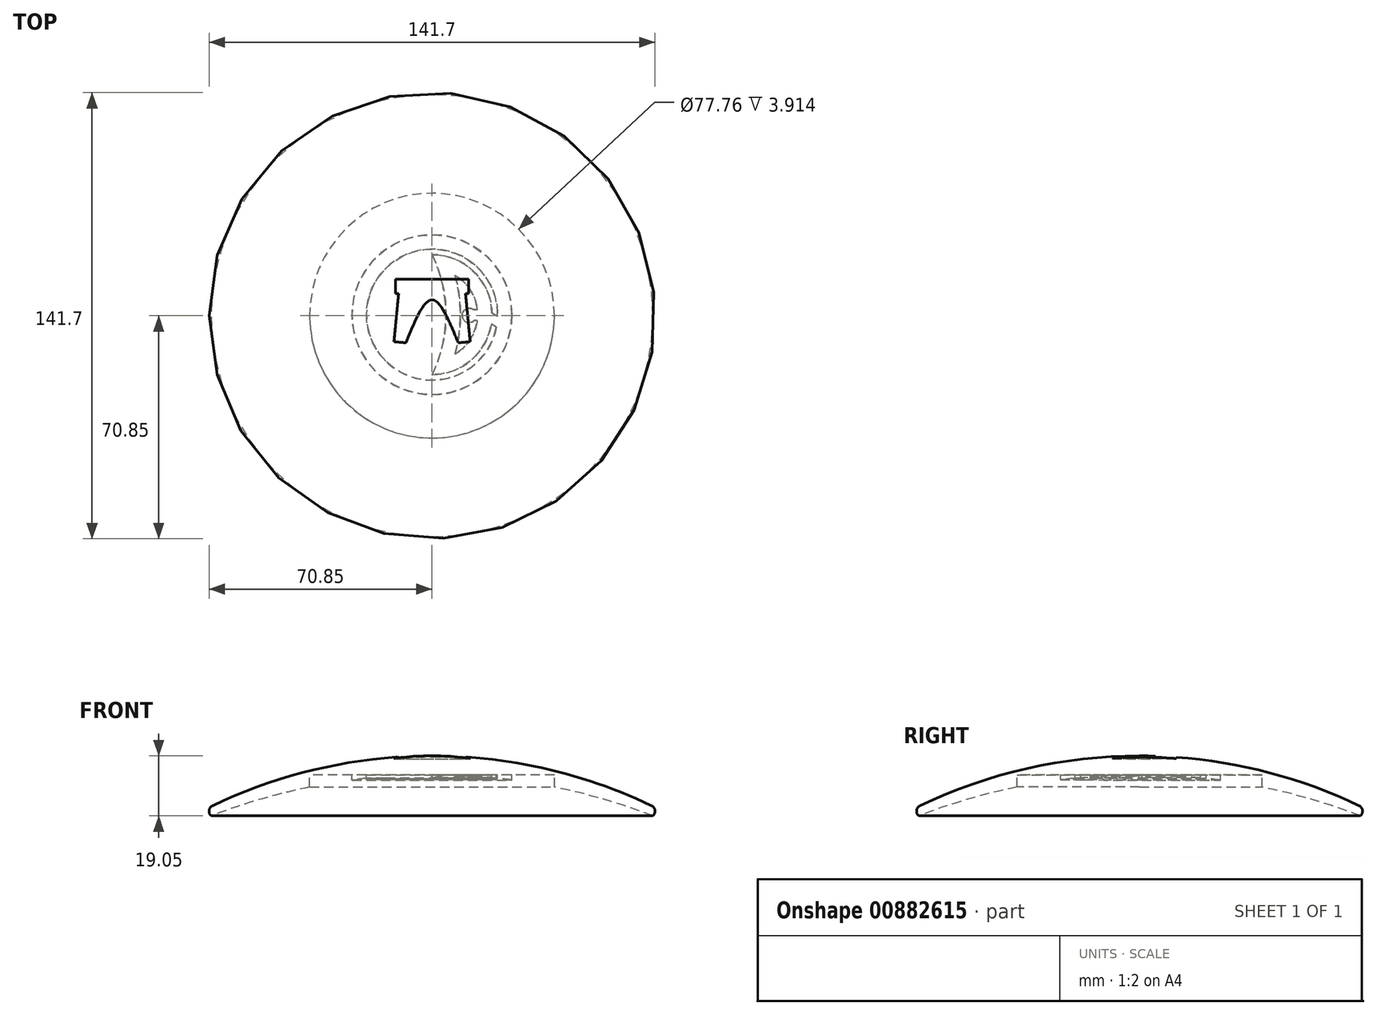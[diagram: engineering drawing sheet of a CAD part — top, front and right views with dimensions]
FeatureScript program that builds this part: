
annotation { "Feature Type Name" : "Feature", "Feature Type Description" : "" }
export const myFeature = defineFeature(function(context is Context, id is Id, definition is map)
    precondition{}
    {
        {
            var Q0;
            Q0=qCreatedBy(makeId("Front.planeOp"),FACE);
            var sketch = newSketch(context, id + "F0", { "sketchPlane" : qUnion([Q0])});
            skLineSegment(sketch, "E0", {"start": v(0, 0) * mm, "end": v(0, 19.05) * mm});
            skLineSegment(sketch, "E1", {"start": v(0, -2.87) * mm, "end": v(-76.2, -2.87) * mm});
            skLineSegment(sketch, "E2", {"start": v(0, 19.05) * mm, "end": v(-91.52, 19.05) * mm});
            skArc(sketch, "E3", {"start": v(0, 19.05) * mm, "mid": v(-39.27, 14.22) * mm, "end": v(-76.2, 0) * mm});
            skLineSegment(sketch, "E4", {"start": v(-76.2, 0) * mm, "end": v(-70.2, 0) * mm});
            skLineSegment(sketch, "E5", {"start": v(0, 19.05) * mm, "end": v(0, 13.05) * mm});
            skLineSegment(sketch, "E6", {"start": v(0, 13.05) * mm, "end": v(-91.4, 13.05) * mm, "construction": true});
            skArc(sketch, "E7", {"start": v(0, 13.05) * mm, "mid": v(-35.7, 9.76) * mm, "end": v(-70.2, 0) * mm});
            skSolve(sketch);
        }
        {
            var Q0;
            Q0=qCreatedBy(makeId("Front.planeOp"),FACE);
            var sketch = newSketch(context, id + "F1", { "sketchPlane" : qUnion([Q0])});
            skLineSegment(sketch, "E8", {"start": v(0, 0) * mm, "end": v(0, 48.31) * mm, "construction": true});
            skSolve(sketch);
        }
        {
            var Q0;
            Q0=makeQuery(id+"F0.imprint","IMPRINT",FACE,{"disambiguationData":[TD([[makeQuery(id+"F0.imprint","IMPRINT",EDGE,{"derivedFrom":sQuery(id+"F0.wireOp",EDGE,"E3")}),1.0]])]});
            var Q1;
            Q1=sQuery(id+"F1.wireOp",EDGE,"E8");
            revolve(context, id + "F2", {"surfaceOperationType" : NewSurfaceOperationType.NEW, "entities" : qUnion([Q0]), "axis" : qUnion([Q1]), "revolveType" : RevolveType.FULL});
        }
        {
            var Q0;
            Q0=makeQuery(id+"F2.opRevolve","SWEPT_EDGE",EDGE,{"disambiguationData":[OSD([sQuery(id+"F0.wireOp",EDGE,"E3"),sQuery(id+"F0.wireOp",EDGE,"E4")])]});
            fillet(context, id + "F3", {"entities" : qUnion([Q0]), "radius" : 2 * mm, "tangentPropagation" : true, "allowEdgeOverflow" : false});
        }
        {
            var Q0;
            Q0=qCreatedBy(makeId("Top.planeOp"),FACE);
            cPlane(context, id + "F4", {"entities" : qUnion([Q0]), "cplaneType" : CPlaneType.OFFSET, "offset" : 18.03 * mm, "width" : 152.4 * mm, "height" : 152.4 * mm});
        }
        {
            var Q0;
            Q0=qCreatedBy(makeId("Top.planeOp"),FACE);
            cPlane(context, id + "F5", {"entities" : qUnion([Q0]), "cplaneType" : CPlaneType.OFFSET, "offset" : 13.06 * mm, "width" : 152.4 * mm, "height" : 152.4 * mm});
        }
        {
            var Q0;
            Q0=qCreatedBy(id+"F5.planeOp",FACE);
            var sketch = newSketch(context, id + "F6", { "sketchPlane" : qUnion([Q0])});
            skLineSegment(sketch, "E9", {"start": v(0, 19.37) * mm, "end": v(0, 0.32) * mm});
            skLineSegment(sketch, "E10.MirrorCS", {"start": v(0, -18.73) * mm, "end": v(0, 0.32) * mm});
            skArc(sketch, "E11", {"start": v(0, -18.73) * mm, "mid": v(19.04, 0.32) * mm, "end": v(0, 19.37) * mm});
            skArc(sketch, "E12", {"start": v(0, -18.73) * mm, "mid": v(4.42, 0.32) * mm, "end": v(0, 19.37) * mm});
            skPoint(sketch, "E13", {"position": v(11.73, 0.32) * mm});
            skCircle(sketch, "E14", {"center": v(0, 0.32) * mm, "radius": 25.4 * mm});
            skCircle(sketch, "E15.0", {"center": v(0, 0.32) * mm, "radius": 20.83 * mm});
            skCircle(sketch, "E16.0", {"center": v(0, 0.32) * mm, "radius": 19.03 * mm});
            skArc(sketch, "E17.0", {"start": v(7.33, -12.16) * mm, "mid": v(8.99, 0.32) * mm, "end": v(7.33, 12.8) * mm});
            skArc(sketch, "E17.1", {"start": v(7.33, -12.16) * mm, "mid": v(14.47, 0.32) * mm, "end": v(7.33, 12.8) * mm});
            skLineSegment(sketch, "E18", {"start": v(11.95, -1.65) * mm, "end": v(11.73, 1.77) * mm});
            skCircle(sketch, "E19", {"center": v(11.84, 0.06) * mm, "radius": 1.72 * mm});
            skArc(sketch, "E20", {"start": v(23.8, -8.54) * mm, "mid": v(19.2, -2.83) * mm, "end": v(11.95, -1.65) * mm});
            skArc(sketch, "E21", {"start": v(24.89, -4.76) * mm, "mid": v(19.36, 0.64) * mm, "end": v(11.73, 1.77) * mm});
            skCircle(sketch, "E22", {"center": v(11.84, 0.06) * mm, "radius": 2.27 * mm});
            skCircle(sketch, "E23", {"center": v(0, 0) * mm, "radius": 38.88 * mm});
            skSolve(sketch);
        }
        {
            var Q0;
            {var subQ0=sQuery(id+"F6.wireOp",EDGE,"E10.MirrorCS");var subQ1=sQuery(id+"F6.wireOp",EDGE,"E9");var subQ2=makeQuery(id+"F6.imprint","INTERSECT",VERTEX,{"derivedFrom":[subQ1,subQ0]});Q0=makeQuery(id+"F6.imprint","IMPRINT",FACE,{"disambiguationData":[TD([[makeQuery(id+"F6.imprint","IMPRINT",EDGE,{"disambiguationData":[TD([[subQ2,1.0]])],"derivedFrom":subQ1}),-1.0]])]});}
            var Q1;
            {var subQ8=sQuery(id+"F6.wireOp",EDGE,"E20");var subQ12=sQuery(id+"F6.wireOp",EDGE,"E15.0");var subQ13=makeQuery(id+"F6.imprint","INTERSECT",VERTEX,{"derivedFrom":[subQ12,subQ8]});Q1=makeQuery(id+"F6.imprint","IMPRINT",FACE,{"disambiguationData":[TD([[makeQuery(id+"F6.imprint","IMPRINT",EDGE,{"disambiguationData":[TD([[subQ13,1.0]])],"derivedFrom":subQ12}),1.0]])]});}
            var Q2;
            {var subQ5=sQuery(id+"F6.wireOp",EDGE,"E17.0");Q2=makeQuery(id+"F6.imprint","IMPRINT",FACE,{"disambiguationData":[TD([[makeQuery(id+"F6.imprint","IMPRINT",EDGE,{"derivedFrom":subQ5}),-1.0]])]});}
            var Q3;
            {var subQ1=sQuery(id+"F6.wireOp",EDGE,"E9");var subQ6=sQuery(id+"F6.wireOp",EDGE,"E10.MirrorCS");var subQ7=makeQuery(id+"F6.imprint","INTERSECT",VERTEX,{"derivedFrom":[subQ1,subQ6]});Q3=makeQuery(id+"F6.imprint","IMPRINT",FACE,{"disambiguationData":[TD([[makeQuery(id+"F6.imprint","IMPRINT",EDGE,{"disambiguationData":[TD([[subQ7,1.0]])],"derivedFrom":subQ1}),1.0]])]});}
            var Q4;
            Q4=makeQuery(id+"F6.imprint","IMPRINT",FACE,{"disambiguationData":[TD([[makeQuery(id+"F6.imprint","IMPRINT",EDGE,{"derivedFrom":sQuery(id+"F6.wireOp",EDGE,"E23")}),1.0]])]});
            extrude(context, id + "F7", {"entities" : qUnion([Q0, Q1, Q2, Q3, Q4]), "operationType" : NewBodyOperationType.REMOVE, "oppositeDirection" : true, "depth" : 25.15 * mm, "offsetDistance" : 25.4 * mm});
        }
        {
            var Q0;
            Q0=qCreatedBy(id+"F4.planeOp",FACE);
            var sketch = newSketch(context, id + "F8", { "sketchPlane" : qUnion([Q0])});
            skLineSegment(sketch, "E24", {"start": v(-11.63, 10.68) * mm, "end": v(0, 10.68) * mm});
            skLineSegment(sketch, "E25", {"start": v(0, 10.68) * mm, "end": v(0, 7.72) * mm});
            skLineSegment(sketch, "E26", {"start": v(0, 7.72) * mm, "end": v(-11.63, 7.72) * mm});
            skLineSegment(sketch, "E27", {"start": v(-11.63, 7.72) * mm, "end": v(-11.63, 10.68) * mm});
            skLineSegment(sketch, "E28", {"start": v(-10.58, 7.72) * mm, "end": v(-11.63, -3.37) * mm});
            skLineSegment(sketch, "E29", {"start": v(-11.63, -3.37) * mm, "end": v(-12.1, -8.28) * mm});
            skLineSegment(sketch, "E30", {"start": v(-12.1, -8.28) * mm, "end": v(-9.99, -8.48) * mm});
            skLineSegment(sketch, "E31", {"start": v(-9.99, -8.48) * mm, "end": v(-8.45, 7.72) * mm});
            skLineSegment(sketch, "E32", {"start": v(-8.45, 7.72) * mm, "end": v(-9.99, -8.48) * mm});
            skLineSegment(sketch, "E33", {"start": v(-9.99, -8.48) * mm, "end": v(-9.02, -8.57) * mm});
            skLineSegment(sketch, "E34", {"start": v(-9.02, -8.57) * mm, "end": v(-7.47, 7.72) * mm});
            skLineSegment(sketch, "E35.MirrorCS", {"start": v(0, 7.72) * mm, "end": v(11.63, 7.72) * mm});
            skLineSegment(sketch, "E36.MirrorCS", {"start": v(11.63, 10.68) * mm, "end": v(0, 10.68) * mm});
            skLineSegment(sketch, "E37.MirrorCS", {"start": v(11.63, 7.72) * mm, "end": v(11.63, 10.68) * mm});
            skLineSegment(sketch, "E38.MirrorCS", {"start": v(10.58, 7.72) * mm, "end": v(11.63, -3.37) * mm});
            skLineSegment(sketch, "E39.MirrorCS", {"start": v(11.63, -3.37) * mm, "end": v(12.1, -8.28) * mm});
            skLineSegment(sketch, "E40.MirrorCS", {"start": v(12.1, -8.28) * mm, "end": v(9.99, -8.48) * mm});
            skLineSegment(sketch, "E41.MirrorCS", {"start": v(9.99, -8.48) * mm, "end": v(8.45, 7.72) * mm});
            skLineSegment(sketch, "E42.MirrorCS", {"start": v(9.02, -8.57) * mm, "end": v(7.47, 7.72) * mm});
            skLineSegment(sketch, "E43.MirrorCS", {"start": v(9.99, -8.48) * mm, "end": v(9.02, -8.57) * mm});
            skLineSegment(sketch, "E44", {"start": v(-11.63, 10.68) * mm, "end": v(-11.63, 11.63) * mm});
            skLineSegment(sketch, "E45", {"start": v(-11.63, 11.63) * mm, "end": v(11.63, 11.63) * mm});
            skLineSegment(sketch, "E46", {"start": v(11.63, 11.63) * mm, "end": v(11.63, 10.68) * mm});
            skLineSegment(sketch, "E47", {"start": v(-11.63, 7.72) * mm, "end": v(-11.63, 7) * mm});
            skLineSegment(sketch, "E48", {"start": v(-11.63, 7) * mm, "end": v(11.63, 7) * mm});
            skLineSegment(sketch, "E49", {"start": v(11.63, 7) * mm, "end": v(11.63, 7.72) * mm});
            skLineSegment(sketch, "E50", {"start": v(-9.02, -8.57) * mm, "end": v(-8.3, -8.64) * mm});
            skLineSegment(sketch, "E51", {"start": v(-8.3, -8.64) * mm, "end": v(-6.74, 7.72) * mm});
            skLineSegment(sketch, "E52.MirrorCS", {"start": v(8.3, -8.64) * mm, "end": v(6.74, 7.72) * mm});
            skLineSegment(sketch, "E53.MirrorCS", {"start": v(9.02, -8.57) * mm, "end": v(8.3, -8.64) * mm});
            skFitSpline(sketch, "E54", {"points": [v(-8.3, -8.64) * mm, v(0, 5.03) * mm, v(8.3, -8.64) * mm], "startDerivative": vector(16.6, 41) * mm, "endDerivative": vector(16.6, -41) * mm});
            skSolve(sketch);
        }
        {
            var Q0;
            Q0 = qSketchRegion(id + "F8", true);
            extrude(context, id + "F9", {"entities" : qUnion([Q0]), "operationType" : NewBodyOperationType.REMOVE, "depth" : 26.67 * mm, "offsetDistance" : 25.4 * mm});
        }
        {
            var Q0;
            Q0=qCreatedBy(id+"F4.planeOp",FACE);
            var sketch = newSketch(context, id + "F10", { "sketchPlane" : qUnion([Q0])});
            skLineSegment(sketch, "E55", {"start": v(9.18, 8.36) * mm, "end": v(-9.24, 8.36) * mm});
            skLineSegment(sketch, "E56", {"start": v(-9.24, 8.36) * mm, "end": v(-9.24, 6.07) * mm});
            skLineSegment(sketch, "E57", {"start": v(-9.24, 6.07) * mm, "end": v(9.18, 6.07) * mm});
            skLineSegment(sketch, "E58", {"start": v(9.18, 6.07) * mm, "end": v(9.18, 8.36) * mm});
            skSolve(sketch);
        }
        {
            var Q0;
            Q0=makeQuery(id+"F10.imprint","IMPRINT",FACE,{"disambiguationData":[TD([[makeQuery(id+"F10.imprint","IMPRINT",EDGE,{"derivedFrom":sQuery(id+"F10.wireOp",EDGE,"E55")}),1.0]])]});
            extrude(context, id + "F11", {"entities" : qUnion([Q0]), "operationType" : NewBodyOperationType.REMOVE, "depth" : 23.37 * mm, "offsetDistance" : 25.4 * mm});
        }
    });
